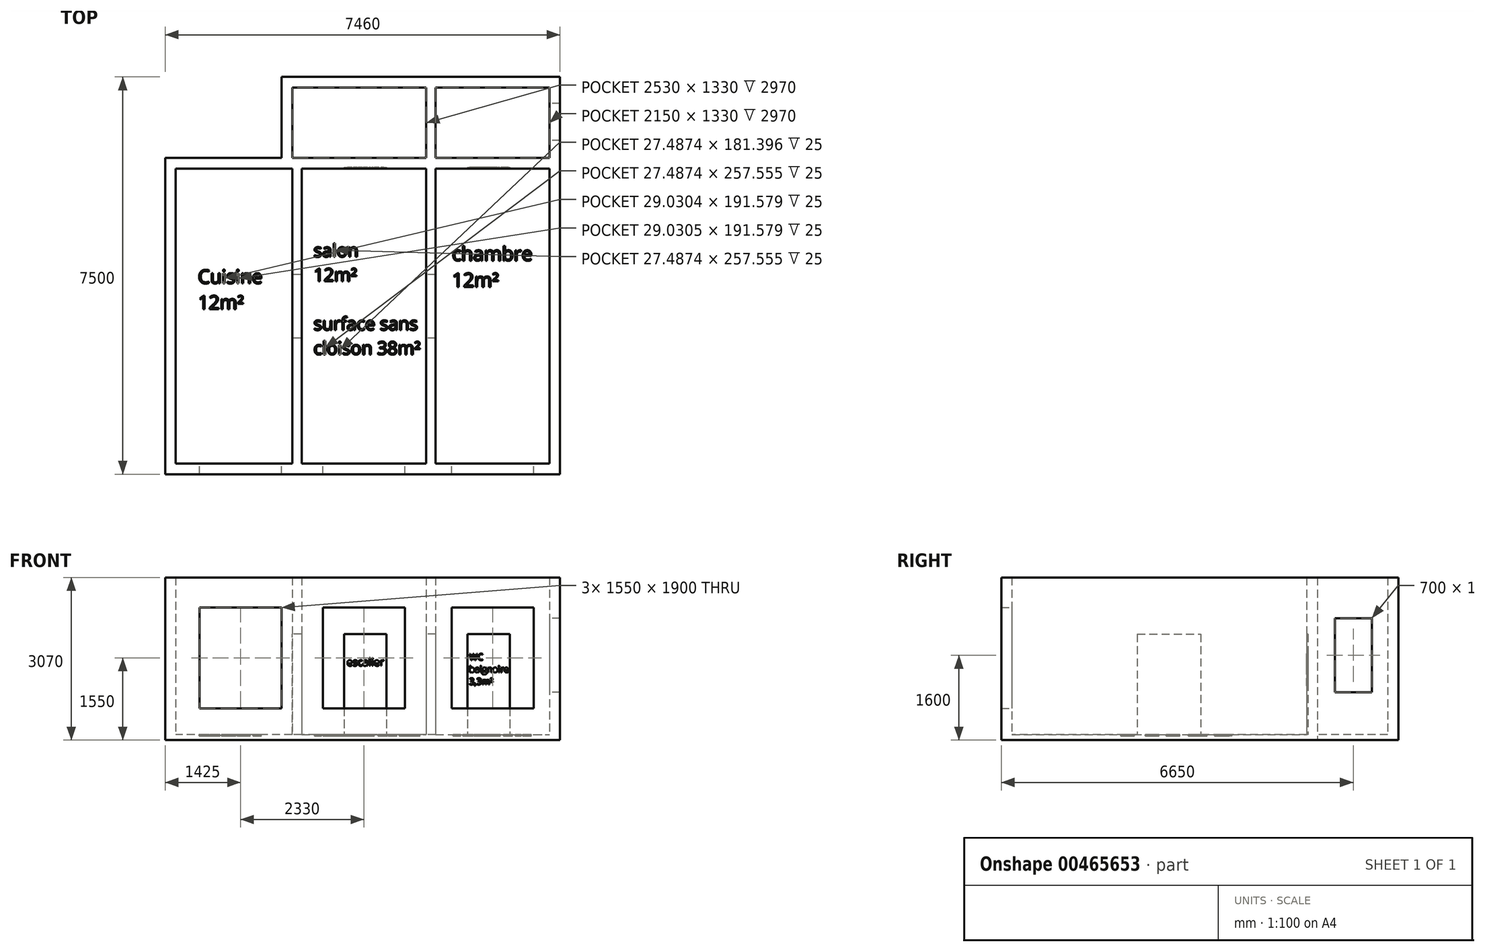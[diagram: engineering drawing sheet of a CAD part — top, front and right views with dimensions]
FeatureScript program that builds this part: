
annotation { "Feature Type Name" : "Feature", "Feature Type Description" : "" }
export const myFeature = defineFeature(function(context is Context, id is Id, definition is map)
    precondition{}
    {
        {
            var Q0;
            Q0=qCreatedBy(makeId("Top.planeOp"),FACE);
            var sketch = newSketch(context, id + "F0", { "sketchPlane" : qUnion([Q0])});
            skLineSegment(sketch, "E0", {"start": v(0, 0) * mm, "end": v(0, 5570) * mm});
            skLineSegment(sketch, "E1", {"start": v(0, 7100) * mm, "end": v(-2150, 7100) * mm});
            skLineSegment(sketch, "E2", {"start": v(-4860, 7100) * mm, "end": v(-4860, 5770) * mm});
            skLineSegment(sketch, "E3", {"start": v(-4860, 5570) * mm, "end": v(-7060, 5570) * mm});
            skLineSegment(sketch, "E4", {"start": v(-7060, 5570) * mm, "end": v(-7060, 0) * mm});
            skLineSegment(sketch, "E5", {"start": v(-7060, 0) * mm, "end": v(-4860, 0) * mm});
            skLineSegment(sketch, "E6.0", {"start": v(-5060, 7300) * mm, "end": v(-5060, 5770) * mm});
            skLineSegment(sketch, "E6.1", {"start": v(-7260, 5770) * mm, "end": v(-7260, -200) * mm});
            skLineSegment(sketch, "E6.2", {"start": v(-7260, -200) * mm, "end": v(200, -200) * mm});
            skLineSegment(sketch, "E6.3", {"start": v(-5060, 5770) * mm, "end": v(-7260, 5770) * mm});
            skLineSegment(sketch, "E6.4", {"start": v(200, -200) * mm, "end": v(200, 7300) * mm});
            skLineSegment(sketch, "E6.5", {"start": v(200, 7300) * mm, "end": v(-5060, 7300) * mm});
            skLineSegment(sketch, "E7", {"start": v(-4680, 5570) * mm, "end": v(-2330, 5570) * mm});
            skLineSegment(sketch, "E8", {"start": v(-4860, 5770) * mm, "end": v(-2330, 5770) * mm});
            skLineSegment(sketch, "E9", {"start": v(-2330, 7100) * mm, "end": v(-2330, 5770) * mm});
            skPoint(sketch, "E9.endSnap0", {"position": v(-2430, 5770) * mm});
            skLineSegment(sketch, "E10", {"start": v(-2150, 7100) * mm, "end": v(-2150, 5770) * mm});
            skLineSegment(sketch, "E11", {"start": v(-4860, 5570) * mm, "end": v(-4860, 0) * mm});
            skLineSegment(sketch, "E12", {"start": v(-4680, 5570) * mm, "end": v(-4680, 0) * mm});
            skLineSegment(sketch, "E13", {"start": v(-2330, 5570) * mm, "end": v(-2330, 0) * mm});
            skLineSegment(sketch, "E14", {"start": v(-2150, 5570) * mm, "end": v(-2150, 0) * mm});
            skLineSegment(sketch, "E15.trimOffspring", {"start": v(-2330, 7100) * mm, "end": v(-4860, 7100) * mm});
            skLineSegment(sketch, "E16.trimOffspring", {"start": v(-2150, 5770) * mm, "end": v(0, 5770) * mm});
            skLineSegment(sketch, "E17.trimOffspring", {"start": v(-2150, 5570) * mm, "end": v(0, 5570) * mm});
            skLineSegment(sketch, "E18.trimOffspring", {"start": v(-4680, 0) * mm, "end": v(-2330, 0) * mm});
            skLineSegment(sketch, "E19.trimOffspring", {"start": v(-2150, 0) * mm, "end": v(0, 0) * mm});
            skLineSegment(sketch, "E20.trimOffspring", {"start": v(0, 5770) * mm, "end": v(0, 7100) * mm});
            skSolve(sketch);
        }
        {
            var Q0;
            Q0 = qSketchRegion(id + "F0", true);
            extrude(context, id + "F1", {"entities" : qUnion([Q0]), "depth" : 2970 * mm});
        }
        {
            var Q0;
            Q0=makeQuery(id+"F1.opExtrude","SWEPT_FACE",FACE,{"disambiguationData":[OSD([sQuery(id+"F0.wireOp",EDGE,"E18.trimOffspring")])]});
            var sketch = newSketch(context, id + "F2", { "sketchPlane" : qUnion([Q0])});
            skLineSegment(sketch, "E21.bottom", {"start": v(300, 2400) * mm, "end": v(1850, 2400) * mm});
            skLineSegment(sketch, "E21.top", {"start": v(300, 500) * mm, "end": v(1850, 500) * mm});
            skLineSegment(sketch, "E21.left", {"start": v(300, 2400) * mm, "end": v(300, 500) * mm});
            skLineSegment(sketch, "E21.right", {"start": v(1850, 2400) * mm, "end": v(1850, 500) * mm});
            skLineSegment(sketch, "E22.bottom", {"start": v(2730, 2400) * mm, "end": v(4280, 2400) * mm});
            skLineSegment(sketch, "E22.top", {"start": v(2730, 500) * mm, "end": v(4280, 500) * mm});
            skLineSegment(sketch, "E22.left", {"start": v(2730, 2400) * mm, "end": v(2730, 500) * mm});
            skLineSegment(sketch, "E22.right", {"start": v(4280, 2400) * mm, "end": v(4280, 500) * mm});
            skLineSegment(sketch, "E23.bottom", {"start": v(5060, 2400) * mm, "end": v(6610, 2400) * mm});
            skLineSegment(sketch, "E23.top", {"start": v(5060, 500) * mm, "end": v(6610, 500) * mm});
            skLineSegment(sketch, "E23.left", {"start": v(5060, 2400) * mm, "end": v(5060, 500) * mm});
            skLineSegment(sketch, "E23.right", {"start": v(6610, 2400) * mm, "end": v(6610, 500) * mm});
            skSolve(sketch);
        }
        {
            var Q0;
            Q0 = qSketchRegion(id + "F2", true);
            extrude(context, id + "F3", {"entities" : qUnion([Q0]), "operationType" : NewBodyOperationType.REMOVE, "endBound" : BoundingType.UP_TO_NEXT, "oppositeDirection" : true, "depth" : 25 * mm});
        }
        {
            var Q0;
            Q0=makeQuery(id+"F1.opExtrude","SWEPT_FACE",FACE,{"disambiguationData":[OSD([sQuery(id+"F0.wireOp",EDGE,"E20.trimOffspring")])]});
            var sketch = newSketch(context, id + "F4", { "sketchPlane" : qUnion([Q0])});
            skLineSegment(sketch, "E24.bottom", {"start": v(-6800, 2200) * mm, "end": v(-6100, 2200) * mm});
            skLineSegment(sketch, "E24.top", {"start": v(-6800, 800) * mm, "end": v(-6100, 800) * mm});
            skLineSegment(sketch, "E24.left", {"start": v(-6800, 2200) * mm, "end": v(-6800, 800) * mm});
            skLineSegment(sketch, "E24.right", {"start": v(-6100, 2200) * mm, "end": v(-6100, 800) * mm});
            skSolve(sketch);
        }
        {
            var Q0;
            Q0 = qSketchRegion(id + "F4", true);
            extrude(context, id + "F5", {"entities" : qUnion([Q0]), "operationType" : NewBodyOperationType.REMOVE, "endBound" : BoundingType.UP_TO_NEXT, "oppositeDirection" : true, "depth" : 25 * mm});
        }
        {
            var Q0;
            Q0=makeQuery(id+"F1.opExtrude","CAP_FACE",FACE,{"disambiguationData":[OSD([sQuery(id+"F0.wireOp",EDGE,"E0"),sQuery(id+"F0.wireOp",EDGE,"E1"),sQuery(id+"F0.wireOp",EDGE,"E2"),sQuery(id+"F0.wireOp",EDGE,"E3"),sQuery(id+"F0.wireOp",EDGE,"E4"),sQuery(id+"F0.wireOp",EDGE,"E5"),sQuery(id+"F0.wireOp",EDGE,"E6.0"),sQuery(id+"F0.wireOp",EDGE,"E6.1"),sQuery(id+"F0.wireOp",EDGE,"E6.2"),sQuery(id+"F0.wireOp",EDGE,"E6.3"),sQuery(id+"F0.wireOp",EDGE,"E6.4"),sQuery(id+"F0.wireOp",EDGE,"E6.5"),sQuery(id+"F0.wireOp",EDGE,"E7"),sQuery(id+"F0.wireOp",EDGE,"E8"),sQuery(id+"F0.wireOp",EDGE,"E9"),sQuery(id+"F0.wireOp",EDGE,"E10"),sQuery(id+"F0.wireOp",EDGE,"E11"),sQuery(id+"F0.wireOp",EDGE,"E12"),sQuery(id+"F0.wireOp",EDGE,"E13"),sQuery(id+"F0.wireOp",EDGE,"E14"),sQuery(id+"F0.wireOp",EDGE,"E15.trimOffspring"),sQuery(id+"F0.wireOp",EDGE,"E16.trimOffspring"),sQuery(id+"F0.wireOp",EDGE,"E17.trimOffspring"),sQuery(id+"F0.wireOp",EDGE,"E18.trimOffspring"),sQuery(id+"F0.wireOp",EDGE,"E19.trimOffspring"),sQuery(id+"F0.wireOp",EDGE,"E20.trimOffspring")])],"isStart":true});
            var sketch = newSketch(context, id + "F6", { "sketchPlane" : qUnion([Q0])});
            skLineSegment(sketch, "E25", {"start": v(-7260, 200) * mm, "end": v(-7260, -5770) * mm});
            skLineSegment(sketch, "E26", {"start": v(-7260, -5770) * mm, "end": v(-5060, -5770) * mm});
            skLineSegment(sketch, "E27", {"start": v(-5060, -5770) * mm, "end": v(-5060, -7300) * mm});
            skLineSegment(sketch, "E28", {"start": v(-5060, -7300) * mm, "end": v(200, -7300) * mm});
            skLineSegment(sketch, "E29", {"start": v(200, -7300) * mm, "end": v(200, 200) * mm});
            skLineSegment(sketch, "E30", {"start": v(200, 200) * mm, "end": v(-7260, 200) * mm});
            skSolve(sketch);
        }
        {
            var Q0;
            Q0 = qSketchRegion(id + "F6", true);
            extrude(context, id + "F7", {"entities" : qUnion([Q0]), "operationType" : NewBodyOperationType.ADD, "depth" : 100 * mm});
        }
        {
            var Q0;
            Q0=makeQuery(id+"F7.boolean.opBoolean","SPLIT",FACE,{"disambiguationData":[TD([makeQuery(id+"F1.opExtrude","SWEPT_FACE",FACE,{"disambiguationData":[OSD([sQuery(id+"F0.wireOp",EDGE,"E7")])]})])],"derivedFrom":makeQuery(id+"F7.opExtrude","CAP_FACE",FACE,{"disambiguationData":[OSD([sQuery(id+"F6.wireOp",EDGE,"E25"),sQuery(id+"F6.wireOp",EDGE,"E26"),sQuery(id+"F6.wireOp",EDGE,"E27"),sQuery(id+"F6.wireOp",EDGE,"E28"),sQuery(id+"F6.wireOp",EDGE,"E29"),sQuery(id+"F6.wireOp",EDGE,"E30")])],"isStart":true})});
            var sketch = newSketch(context, id + "F8", { "sketchPlane" : qUnion([Q0])});
            skText(sketch, "E31", { "text": "Cuisine\n12m²", "fontName": "OpenSans-Regular.ttf"});
            skText(sketch, "E32", { "text": "salon\n12m²\n\nsurface sans \ncloison 38m²", "fontName": "OpenSans-Regular.ttf"});
            skText(sketch, "E33", { "text": "chambre\n12m²", "fontName": "OpenSans-Regular.ttf"});
            const initialGuessF8  = {"E31": [-6.6389, 3.40218, 1, 0, 0.25775], "E32": [-4.45594, 3.90376, 1, 0, 0.24405], "E33": [-1.84027, 3.83202, 1, 0, 0.26284]};
            skSetInitialGuess(sketch, initialGuessF8);
            skSolve(sketch);
        }
        {
            var Q0;
            Q0=makeQuery(id+"F1.opExtrude","SWEPT_FACE",FACE,{"disambiguationData":[OSD([sQuery(id+"F0.wireOp",EDGE,"E11")])]});
            var sketch = newSketch(context, id + "F9", { "sketchPlane" : qUnion([Q0])});
            skLineSegment(sketch, "E34.bottom", {"start": v(-3570, 0) * mm, "end": v(-2370, 0) * mm});
            skLineSegment(sketch, "E34.top", {"start": v(-3570, 1900) * mm, "end": v(-2370, 1900) * mm});
            skLineSegment(sketch, "E34.left", {"start": v(-3570, 0) * mm, "end": v(-3570, 1900) * mm});
            skLineSegment(sketch, "E34.right", {"start": v(-2370, 0) * mm, "end": v(-2370, 1900) * mm});
            skSolve(sketch);
        }
        {
            var Q0;
            Q0 = qSketchRegion(id + "F9", true);
            extrude(context, id + "F10", {"entities" : qUnion([Q0]), "operationType" : NewBodyOperationType.REMOVE, "oppositeDirection" : true, "depth" : 3000 * mm});
        }
        {
            var Q0;
            Q0 = qSketchRegion(id + "F8", true);
            extrude(context, id + "F11", {"entities" : qUnion([Q0]), "operationType" : NewBodyOperationType.REMOVE, "oppositeDirection" : true, "depth" : 25 * mm});
        }
        {
            var Q0;
            Q0=makeQuery(id+"F1.opExtrude","SWEPT_FACE",FACE,{"disambiguationData":[OSD([sQuery(id+"F0.wireOp",EDGE,"E17.trimOffspring")])]});
            var sketch = newSketch(context, id + "F12", { "sketchPlane" : qUnion([Q0])});
            skLineSegment(sketch, "E35.bottom", {"start": v(-1550, 1900) * mm, "end": v(-750, 1900) * mm});
            skLineSegment(sketch, "E35.top", {"start": v(-1550, 0) * mm, "end": v(-750, 0) * mm});
            skLineSegment(sketch, "E35.left", {"start": v(-1550, 1900) * mm, "end": v(-1550, 0) * mm});
            skLineSegment(sketch, "E35.right", {"start": v(-750, 1900) * mm, "end": v(-750, 0) * mm});
            skText(sketch, "E36", { "text": "WC\nbaignoire\n3,3m²", "fontName": "OpenSans-Regular.ttf"});
            skLineSegment(sketch, "E37.bottom", {"start": v(-3880, 1900) * mm, "end": v(-3080, 1900) * mm});
            skLineSegment(sketch, "E37.top", {"start": v(-3880, 0) * mm, "end": v(-3080, 0) * mm});
            skLineSegment(sketch, "E37.left", {"start": v(-3880, 1900) * mm, "end": v(-3880, 0) * mm});
            skLineSegment(sketch, "E37.right", {"start": v(-3080, 1900) * mm, "end": v(-3080, 0) * mm});
            skText(sketch, "E38", { "text": "escalier", "fontName": "OpenSans-Regular.ttf"});
            const initialGuessF12  = {"E36": [-1.51617, 1.40831, 1, 0, 0.12218], "E38": [-3.83018, 1.30125, 1, 0, 0.14298]};
            skSetInitialGuess(sketch, initialGuessF12);
            skSolve(sketch);
        }
        {
            var Q0;
            Q0 = qSketchRegion(id + "F12", true);
            extrude(context, id + "F13", {"entities" : qUnion([Q0]), "operationType" : NewBodyOperationType.REMOVE, "oppositeDirection" : true, "depth" : 25 * mm});
        }
    });
